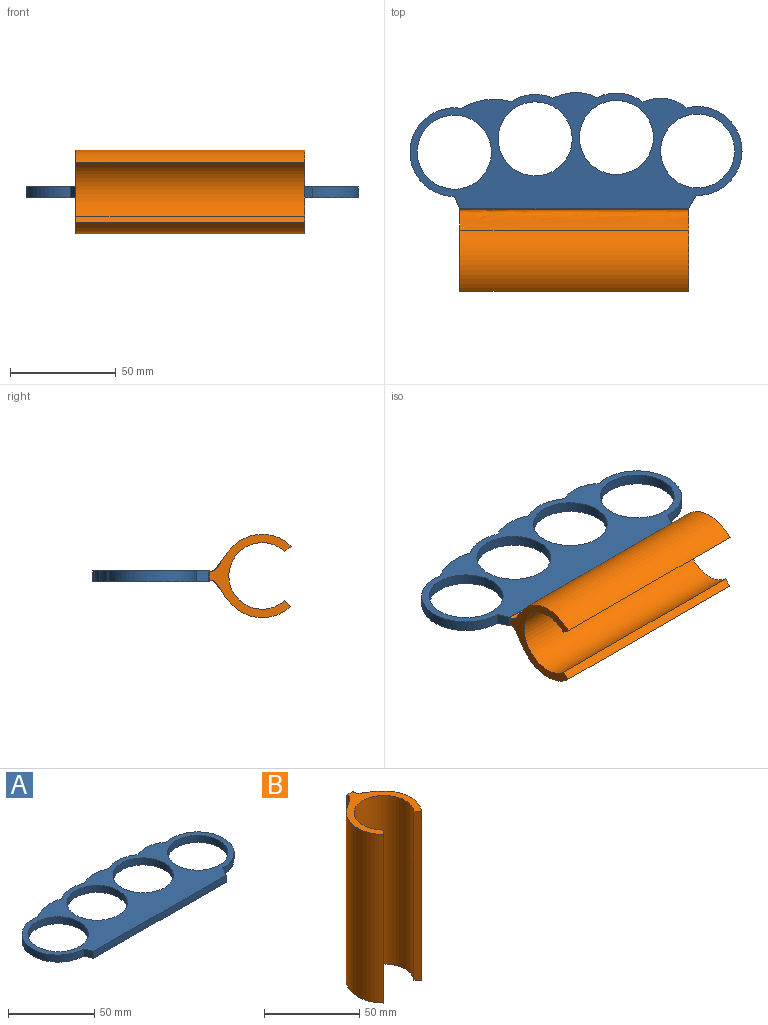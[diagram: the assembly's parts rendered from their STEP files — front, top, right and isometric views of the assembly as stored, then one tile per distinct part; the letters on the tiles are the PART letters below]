
ASSEMBLY  parts=2 mates=1
PART A: 16 faces, bbox 157x55.5x5 mm
  f0: cylinder r=20.99mm len=19.75mm, axis (0,0,-1), area 103.2mm2, adj f1,f12,f14,f15
  f1: extruded ~23.35x5mm, area 121.3mm2, adj f0,f2,f14,f15
  f2: cylinder r=20.99mm len=41.97mm, axis (0,0,-1), area 346.2mm2, adj f1,f3,f14,f15
  f3: plane 5.84x5mm, normal (-0.91,-0.41,0), area 32mm2, adj f2,f4,f14,f15
  f4: plane 108.26x5mm, normal (0,-1,0), area 541.3mm2, adj f3,f5,f14,f15
  f5: plane 6.41x5mm, normal (0.87,-0.5,0), area 37mm2, adj f4,f6,f14,f15
  f6: cylinder r=20.99mm len=41.97mm, axis (0,0,-1), area 358mm2, adj f5,f7,f14,f15
  f7: extruded ~20.82x5mm, area 110.8mm2, adj f6,f8,f14,f15
  f8: cylinder r=20.99mm len=21.83mm, axis (0,0,-1), area 115.3mm2, adj f7,f12,f14,f15
  f9: cylinder r=17.5mm len=35mm, axis (0,0,-1), area 549.8mm2, adj f14,f15
  f10: cylinder r=17.5mm len=35mm, axis (0,0,-1), area 549.8mm2, adj f14,f15
  f11: cylinder r=17.5mm len=35mm, axis (0,0,-1), area 549.8mm2, adj f14,f15
  f12: extruded ~20.93x5mm, area 108.5mm2, adj f0,f8,f14,f15
  f13: cylinder r=17.5mm len=35mm, axis (0,0,-1), area 549.8mm2, adj f14,f15
  f14: plane 157.05x55.47mm, normal (0,0,1), area 3525.6mm2, adj f0,f1,f2,f3,f4,f5,f6,f7
  f15: plane 157.05x55.47mm, normal (0,0,-1), area 3525.6mm2, adj f0,f1,f2,f3,f4,f5,f6,f7
PART B: 10 faces, bbox 39.5x39x108.3 mm
  f0: plane 108.25x5mm, normal (0,1,0), area 541.3mm2, adj f1,f7,f8,f9
  f1: extruded ~108.25x10.66mm, area 1667.4mm2, adj f0,f2,f8,f9
  f2: cylinder r=19.73mm len=108.25mm, axis (0,0,-1), area 3506.8mm2, adj f1,f3,f8,f9
  f3: plane 108.25x3.15mm, normal (0.78,-0.63,0), area 436.9mm2, adj f2,f4,f8,f9
  f4: cylinder r=15.73mm len=108.25mm, axis (0,0,-1), area 7871.9mm2, adj f3,f5,f8,f9
  f5: plane 108.25x2.91mm, normal (-0.73,-0.69,0), area 434mm2, adj f4,f6,f8,f9
  f6: cylinder r=19.73mm len=108.25mm, axis (0,0,-1), area 3616.8mm2, adj f5,f7,f8,f9
  f7: extruded ~108.25x9.59mm, area 1522.2mm2, adj f0,f6,f8,f9
  f8: plane 39.46x38.95mm, normal (0,0,1), area 373.5mm2, adj f0,f1,f2,f3,f4,f5,f6,f7
  f9: plane 39.46x38.95mm, normal (0,0,-1), area 373.5mm2, adj f0,f1,f2,f3,f4,f5,f6,f7
PLACE A t=(-0.07,0.08,2.36)mm
PLACE B rot(axis=(0,1,0),90deg) t=(-61.67,-53.52,-35.76)mm
MATE parallel B.f0 <-> A.f4  axis (0,1,0) through (-7.54,-6.68,2.5)mm
